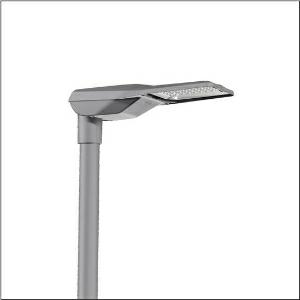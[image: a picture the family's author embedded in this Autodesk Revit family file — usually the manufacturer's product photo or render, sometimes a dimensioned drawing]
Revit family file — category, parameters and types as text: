
# Revit family: streetlight_sl_21_iq_mini___stw1_0a_5xe2e41g08hb_6f26
name_source: partatom
category: Lighting Fixtures
units: mm (PartAtom-declared; Revit-internal decimal feet)

## family parameters
Cut with Voids When Loaded = No
Host = Face
Light Source = No
Part Type = Normal
Room Calculation Point = No
Round Connector Dimension = Use Diameter
Shared = No

## types (1)
- --- (1 x LED, 9860 lm, 70.9 W, 4000K)
    Apparent Load = 71 VA
    CIE Flux Codes = 38 75 98 100 100
    Color Rendering = 70
    Color Temperature = 4000K
    Default Elevation = 1800 mm
    Description = Streetlight SL 21 iQ mini, mast luminaire, primary light control with lens, of PMMA, primary optical cover: cover, of toughened safety glass, transparent, light distribution: STW1.0a, light emission: direct distribution, primary light characteristic: asymmetric, installation type: post-top, side-entry, LED, High Power LED, rated luminous flux: 9.860lm, luminous efficacy: 139lm/W, light colour: 740, colour temperature: 4000K, control gear: iQ Street-Remote, control: Street-Remote, Auto-Match, Temp-Guard, Lumen-Switch, Night-Set, Smart-Wire, Light-Fading, Desk-Remote (wireless, voltage-free reading and setting of iQ features in the workshop via application-optimized NFC function/RFID function), optimised constant luminous flux control (CLO 2.0), pre-setting: linear dimming characteristic, mains connection: 220..240V, AC, 50/60Hz, start of lifetime: 71W, end of service life: 75W, reduction: 31W, luminaire housing, of diecast aluminium, powder-coated, SITECO metallic grey (DB 702S), corrosivity category C5 high according to DIN EN ISO 12944, please order mast flange separately, inclination adjustable: 0°, 5°, 10°, 15°, sealing non-destructively replaceable, multi-level sealing system, length: 628mm, width: 235mm, height: 110mm, mast flange for spigot size: 42mm (side-entry): 5XC10008XM4, 60/48mm (side-entry/post-top): 5XC10108XM2, 76/60mm (side-entry/post-top): 5XC10108XM1, mounting height: 4..8m, protection rating (complete): IP66, insulation class (complete): insulation class II (safety insulation), certification: CE, ENEC, ENEC+, VDE, impact resistance: IK10, permissible operating ambient temperature for outdoor applications: -40..+50°C, standard-compliant lighting for roads and squares, packaging unit: 1 piece

Light Distribution: STW1.0a
    Height = 110 mm
    Lamp = 1 x LED
    Lamp Light Flux = 9860 lm
    Lamp Power = 70.9 W
    Lamp count = 1
    Length = 625 mm
    Luminous efficacy = 139 lm/W
    Manufacturer = Siteco
    ModVariant = No
    Model = 5XE2E41G08HB
    Number of Poles = 1
    OnlyDefault = Yes
    Power Factor = 1
    Product Name = Streetlight SL 21 iQ mini | STW1.0a
    Product group = mast luminaire | pylon top
    ProductGroupID = 6100
    Protection Class = Protection class II
    Protection Degree = IP 66
    RLX_Detail_Level = 1
    RLX_Emergency_Light_Flux = 0 lm
    RLX_Emergency_Type = 0
    RLX_Emergency_Type_DB = No
    RlxData = <blob elided: 26337 chars, md5=fdefd07c>
    Socket = socket
    Standby Power = 0 W
    System Light Flux = 9860 lm
    System Power = 71 W
    Type Comments = factory setting: luminous flux: 100 % | dim-lin: 254 | 711 mA
    Type Image = l_1003519.jpg
    URL = http://relux.com
    VarID = @adj_157223
    Voltage = 0 V
    Weight = 0.00 kg
    Width = 234 mm

## geometry (parser evidence)
native form markers: Blend x4, Sweep x12
no freeform markers — native parametric forms only
